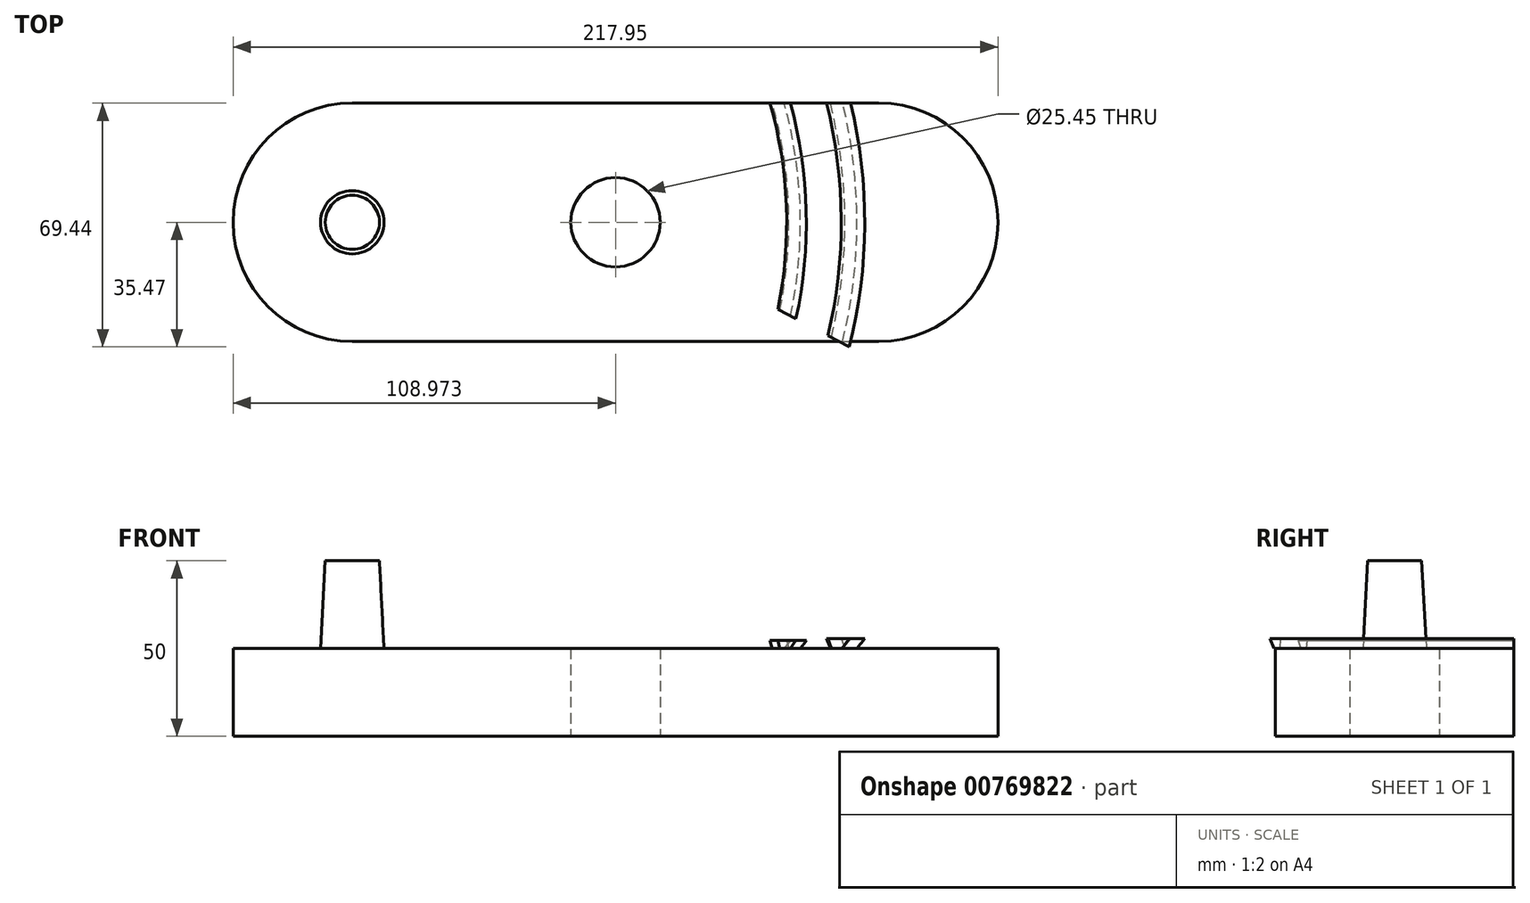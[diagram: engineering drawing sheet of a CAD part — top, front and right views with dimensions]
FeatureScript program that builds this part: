
annotation { "Feature Type Name" : "Feature", "Feature Type Description" : "" }
export const myFeature = defineFeature(function(context is Context, id is Id, definition is map)
    precondition{}
    {
        {
            var Q0;
            Q0=qCreatedBy(makeId("Top.planeOp"),FACE);
            var sketch = newSketch(context, id + "F0", { "sketchPlane" : qUnion([Q0])});
            skLineSegment(sketch, "E0.bottom", {"start": v(-71.22, 30.3) * mm, "end": v(78.78, 30.3) * mm});
            skLineSegment(sketch, "E0.top", {"start": v(-71.22, -37.65) * mm, "end": v(78.78, -37.65) * mm});
            skLineSegment(sketch, "E0.left", {"start": v(-71.22, 30.3) * mm, "end": v(-71.22, -37.65) * mm});
            skLineSegment(sketch, "E0.right", {"start": v(78.78, 30.3) * mm, "end": v(78.78, -37.65) * mm});
            skArc(sketch, "E1", {"start": v(-71.22, 30.3) * mm, "mid": v(-105.2, -3.68) * mm, "end": v(-71.22, -37.65) * mm});
            skArc(sketch, "E2", {"start": v(78.78, -37.65) * mm, "mid": v(112.76, -3.68) * mm, "end": v(78.78, 30.3) * mm});
            skCircle(sketch, "E3", {"center": v(-71.22, -3.68) * mm, "radius": 10.34 * mm});
            skCircle(sketch, "E4", {"center": v(3.78, -3.68) * mm, "radius": 12.72 * mm});
            skPoint(sketch, "E4.centerSnap0", {"position": v(3.78, 30.3) * mm});
            skSolve(sketch);
        }
        {
            var Q0;
            Q0=makeQuery(id+"F0.imprint","IMPRINT",FACE,{"disambiguationData":[TD([[makeQuery(id+"F0.imprint","IMPRINT",EDGE,{"derivedFrom":sQuery(id+"F0.wireOp",EDGE,"E0.right")}),1.0]])]});
            var Q1;
            {var subQ5=sQuery(id+"F0.wireOp",EDGE,"E0.bottom");Q1=makeQuery(id+"F0.imprint","IMPRINT",FACE,{"disambiguationData":[TD([[makeQuery(id+"F0.imprint","IMPRINT",EDGE,{"derivedFrom":subQ5}),-1.0]])]});}
            var Q2;
            {var subQ0=sQuery(id+"F0.wireOp",EDGE,"E3");var subQ1=sQuery(id+"F0.wireOp",EDGE,"E0.left");var subQ2=makeQuery(id+"F0.imprint","INTERSECT",VERTEX,{"disambiguationData":[OD(0.0)],"derivedFrom":[subQ1,subQ0]});Q2=makeQuery(id+"F0.imprint","IMPRINT",FACE,{"disambiguationData":[TD([[makeQuery(id+"F0.imprint","IMPRINT",EDGE,{"disambiguationData":[TD([[subQ2,-1.0]])],"derivedFrom":subQ1}),-1.0]])]});}
            var Q3;
            {var subQ0=sQuery(id+"F0.wireOp",EDGE,"E1");Q3=makeQuery(id+"F0.imprint","IMPRINT",FACE,{"disambiguationData":[TD([[makeQuery(id+"F0.imprint","IMPRINT",EDGE,{"derivedFrom":subQ0}),1.0]])]});}
            var Q4;
            {var subQ0=sQuery(id+"F0.wireOp",EDGE,"E3");var subQ1=sQuery(id+"F0.wireOp",EDGE,"E0.left");var subQ2=makeQuery(id+"F0.imprint","INTERSECT",VERTEX,{"disambiguationData":[OD(0.0)],"derivedFrom":[subQ1,subQ0]});Q4=makeQuery(id+"F0.imprint","IMPRINT",FACE,{"disambiguationData":[TD([[makeQuery(id+"F0.imprint","IMPRINT",EDGE,{"disambiguationData":[TD([[subQ2,-1.0]])],"derivedFrom":subQ1}),1.0]])]});}
            extrude(context, id + "F1", {"entities" : qUnion([Q0, Q1, Q2, Q3, Q4]), "depth" : 25 * mm, "offsetDistance" : 25 * mm});
        }
        {
            var Q0;
            {var subQ0=sQuery(id+"F0.wireOp",EDGE,"E3");var subQ1=sQuery(id+"F0.wireOp",EDGE,"E0.left");var subQ2=makeQuery(id+"F0.imprint","INTERSECT",VERTEX,{"disambiguationData":[OD(0.0)],"derivedFrom":[subQ1,subQ0]});Q0=makeQuery(id+"F0.imprint","IMPRINT",FACE,{"disambiguationData":[TD([[makeQuery(id+"F0.imprint","IMPRINT",EDGE,{"disambiguationData":[TD([[subQ2,-1.0]])],"derivedFrom":subQ1}),1.0]])]});}
            var Q1;
            {var subQ0=sQuery(id+"F0.wireOp",EDGE,"E3");var subQ1=sQuery(id+"F0.wireOp",EDGE,"E0.left");var subQ2=makeQuery(id+"F0.imprint","INTERSECT",VERTEX,{"disambiguationData":[OD(0.0)],"derivedFrom":[subQ1,subQ0]});Q1=makeQuery(id+"F0.imprint","IMPRINT",FACE,{"disambiguationData":[TD([[makeQuery(id+"F0.imprint","IMPRINT",EDGE,{"disambiguationData":[TD([[subQ2,-1.0]])],"derivedFrom":subQ1}),-1.0]])]});}
            extrude(context, id + "F2", {"entities" : qUnion([Q0, Q1]), "operationType" : NewBodyOperationType.ADD, "oppositeDirection" : true, "depth" : -50 * mm, "offsetDistance" : 25 * mm, "hasDraft" : true, "draftAngle" : 3 * degree, "draftPullDirection" : true});
        }
        {
            var Q0;
            Q0=makeQuery(id+"F1.opExtrude","SWEPT_FACE",FACE,{"disambiguationData":[OSD([sQuery(id+"F0.wireOp",EDGE,"E0.bottom")])]});
            var sketch = newSketch(context, id + "F3", { "sketchPlane" : qUnion([Q0])});
            skLineSegment(sketch, "E5.bottom", {"start": v(-51.86, 25) * mm, "end": v(-48.43, 25) * mm});
            skLineSegment(sketch, "E5.top", {"start": v(-53.62, 27.25) * mm, "end": v(-47.8, 27.25) * mm});
            skLineSegment(sketch, "E6", {"start": v(-68.5, 25) * mm, "end": v(-64.98, 25) * mm});
            skLineSegment(sketch, "E7", {"start": v(-64.98, 25) * mm, "end": v(-63.9, 27.82) * mm});
            skLineSegment(sketch, "E8", {"start": v(-63.9, 27.82) * mm, "end": v(-70.79, 27.82) * mm});
            skLineSegment(sketch, "E9", {"start": v(-70.79, 27.82) * mm, "end": v(-68.5, 25) * mm});
            skLineSegment(sketch, "E10", {"start": v(-48.43, 25) * mm, "end": v(-47.8, 27.25) * mm});
            skLineSegment(sketch, "E11", {"start": v(-53.62, 27.25) * mm, "end": v(-51.86, 25) * mm});
            skSolve(sketch);
        }
        {
            var Q0;
            Q0=makeQuery(id+"F3.imprint","IMPRINT",FACE,{"disambiguationData":[TD([[makeQuery(id+"F3.imprint","IMPRINT",EDGE,{"derivedFrom":sQuery(id+"F3.wireOp",EDGE,"E6")}),-1.0]])]});
            var Q1;
            Q1=makeQuery(id+"F3.imprint","IMPRINT",FACE,{"disambiguationData":[TD([[makeQuery(id+"F3.imprint","IMPRINT",EDGE,{"derivedFrom":sQuery(id+"F3.wireOp",EDGE,"E5.top")}),-1.0]])]});
            var Q2;
            Q2=makeQuery(id+"F2.opExtrude","CAP_EDGE",EDGE,{"disambiguationData":[OSD([sQuery(id+"F0.wireOp",EDGE,"E3")])],"isStart":false});
            revolve(context, id + "F4", {"operationType" : NewBodyOperationType.ADD, "surfaceOperationType" : NewSurfaceOperationType.NEW, "entities" : qUnion([Q0, Q1]), "axis" : qUnion([Q2]), "revolveType" : RevolveType.ONE_DIRECTION, "oppositeDirection" : true, "angle" : 27.51 * degree});
        }
    });
